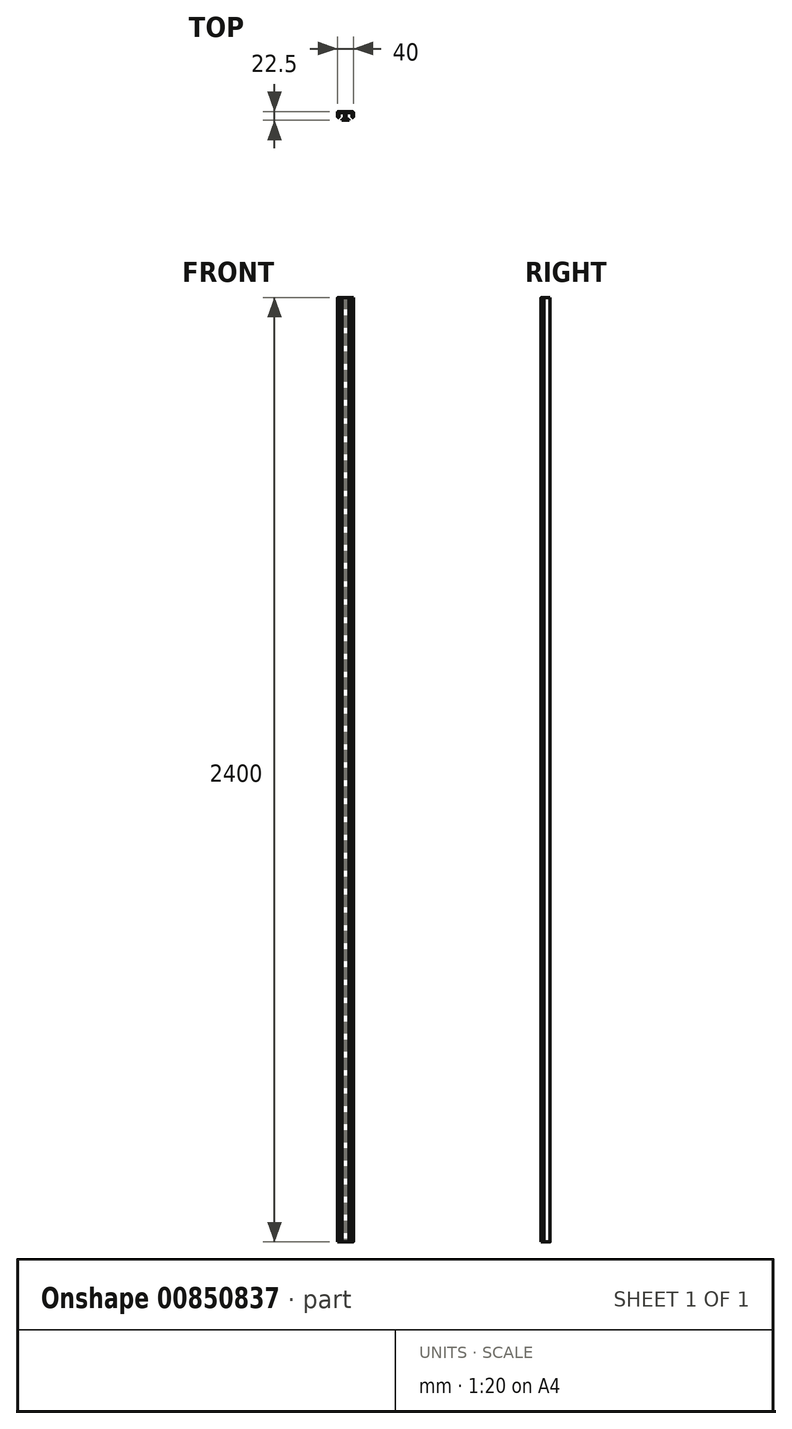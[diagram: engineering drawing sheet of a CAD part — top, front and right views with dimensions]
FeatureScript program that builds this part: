
annotation { "Feature Type Name" : "Feature", "Feature Type Description" : "" }
export const myFeature = defineFeature(function(context is Context, id is Id, definition is map)
    precondition{}
    {
        {
            var Q0;
            Q0=qCreatedBy(makeId("Top.planeOp"),FACE);
            var sketch = newSketch(context, id + "F0", { "sketchPlane" : qUnion([Q0])});
            skLineSegment(sketch, "E0", {"start": v(-20, 10) * mm, "end": v(20, 10) * mm});
            skLineSegment(sketch, "E1", {"start": v(20, 10) * mm, "end": v(20, -5) * mm});
            skLineSegment(sketch, "E2", {"start": v(-20, 10) * mm, "end": v(-20, -5) * mm});
            skLineSegment(sketch, "E3.0", {"start": v(-17, 7) * mm, "end": v(-17, -5) * mm});
            skLineSegment(sketch, "E3.1", {"start": v(-17, 7) * mm, "end": v(-2, 7) * mm});
            skLineSegment(sketch, "E3.2", {"start": v(17, 7) * mm, "end": v(17, -5) * mm});
            skLineSegment(sketch, "E4", {"start": v(-20, -5) * mm, "end": v(-17, -5) * mm});
            skLineSegment(sketch, "E5", {"start": v(17, -5) * mm, "end": v(20, -5) * mm});
            skLineSegment(sketch, "E6", {"start": v(-2, 7) * mm, "end": v(-2, -9.5) * mm});
            skLineSegment(sketch, "E7", {"start": v(-2, -9.5) * mm, "end": v(-8.5, -9.5) * mm});
            skLineSegment(sketch, "E8", {"start": v(-8.5, -9.5) * mm, "end": v(-8.5, -12.5) * mm});
            skLineSegment(sketch, "E9", {"start": v(-8.5, -12.5) * mm, "end": v(0, -12.5) * mm});
            skLineSegment(sketch, "E10.MirrorCS", {"start": v(8.5, -12.5) * mm, "end": v(0, -12.5) * mm});
            skLineSegment(sketch, "E11.MirrorCS", {"start": v(8.5, -9.5) * mm, "end": v(8.5, -12.5) * mm});
            skLineSegment(sketch, "E12.MirrorCS", {"start": v(2, 7) * mm, "end": v(2, -9.5) * mm});
            skLineSegment(sketch, "E13.MirrorCS", {"start": v(2, -9.5) * mm, "end": v(8.5, -9.5) * mm});
            skLineSegment(sketch, "E14.trimOffspring", {"start": v(2, 7) * mm, "end": v(17, 7) * mm});
            skSolve(sketch);
        }
        {
            var Q0;
            Q0 = qSketchRegion(id + "F0", true);
            extrude(context, id + "F1", {"entities" : qUnion([Q0]), "depth" : 2400 * mm, "offsetDistance" : 25 * mm});
        }
        {
            var Q0;
            Q0=makeQuery(id+"F1.opExtrude","SWEPT_EDGE",EDGE,{"disambiguationData":[OSD([sQuery(id+"F0.wireOp",EDGE,"E0"),sQuery(id+"F0.wireOp",EDGE,"E2")])]});
            var Q1;
            Q1=makeQuery(id+"F1.opExtrude","SWEPT_EDGE",EDGE,{"disambiguationData":[OSD([sQuery(id+"F0.wireOp",EDGE,"E0"),sQuery(id+"F0.wireOp",EDGE,"E1")])]});
            fillet(context, id + "F2", {"entities" : qUnion([Q0, Q1]), "radius" : 2 * mm, "tangentPropagation" : true, "allowEdgeOverflow" : false});
        }
        {
            var Q0;
            Q0=makeQuery(id+"F1.opExtrude","SWEPT_EDGE",EDGE,{"disambiguationData":[OSD([sQuery(id+"F0.wireOp",EDGE,"E2"),sQuery(id+"F0.wireOp",EDGE,"E4")])]});
            var Q1;
            Q1=makeQuery(id+"F1.opExtrude","SWEPT_EDGE",EDGE,{"disambiguationData":[OSD([sQuery(id+"F0.wireOp",EDGE,"E3.0"),sQuery(id+"F0.wireOp",EDGE,"E4")])]});
            var Q2;
            Q2=makeQuery(id+"F1.opExtrude","SWEPT_EDGE",EDGE,{"disambiguationData":[OSD([sQuery(id+"F0.wireOp",EDGE,"E3.0"),sQuery(id+"F0.wireOp",EDGE,"E3.1")])]});
            var Q3;
            Q3=makeQuery(id+"F1.opExtrude","SWEPT_EDGE",EDGE,{"disambiguationData":[OSD([sQuery(id+"F0.wireOp",EDGE,"E8"),sQuery(id+"F0.wireOp",EDGE,"E9")])]});
            var Q4;
            Q4=makeQuery(id+"F1.opExtrude","SWEPT_EDGE",EDGE,{"disambiguationData":[OSD([sQuery(id+"F0.wireOp",EDGE,"E10.MirrorCS"),sQuery(id+"F0.wireOp",EDGE,"E11.MirrorCS")])]});
            var Q5;
            Q5=makeQuery(id+"F1.opExtrude","SWEPT_EDGE",EDGE,{"disambiguationData":[OSD([sQuery(id+"F0.wireOp",EDGE,"E11.MirrorCS"),sQuery(id+"F0.wireOp",EDGE,"E13.MirrorCS")])]});
            var Q6;
            Q6=makeQuery(id+"F1.opExtrude","SWEPT_EDGE",EDGE,{"disambiguationData":[OSD([sQuery(id+"F0.wireOp",EDGE,"E12.MirrorCS"),sQuery(id+"F0.wireOp",EDGE,"E14.trimOffspring")])]});
            var Q7;
            Q7=makeQuery(id+"F1.opExtrude","SWEPT_EDGE",EDGE,{"disambiguationData":[OSD([sQuery(id+"F0.wireOp",EDGE,"E3.2"),sQuery(id+"F0.wireOp",EDGE,"E5")])]});
            var Q8;
            Q8=makeQuery(id+"F1.opExtrude","SWEPT_EDGE",EDGE,{"disambiguationData":[OSD([sQuery(id+"F0.wireOp",EDGE,"E1"),sQuery(id+"F0.wireOp",EDGE,"E5")])]});
            var Q9;
            Q9=makeQuery(id+"F1.opExtrude","SWEPT_EDGE",EDGE,{"disambiguationData":[OSD([sQuery(id+"F0.wireOp",EDGE,"E3.2"),sQuery(id+"F0.wireOp",EDGE,"E14.trimOffspring")])]});
            var Q10;
            Q10=makeQuery(id+"F1.opExtrude","SWEPT_EDGE",EDGE,{"disambiguationData":[OSD([sQuery(id+"F0.wireOp",EDGE,"E3.1"),sQuery(id+"F0.wireOp",EDGE,"E6")])]});
            var Q11;
            Q11=makeQuery(id+"F1.opExtrude","SWEPT_EDGE",EDGE,{"disambiguationData":[OSD([sQuery(id+"F0.wireOp",EDGE,"E7"),sQuery(id+"F0.wireOp",EDGE,"E8")])]});
            var Q12;
            Q12=makeQuery(id+"F1.opExtrude","SWEPT_EDGE",EDGE,{"disambiguationData":[OSD([sQuery(id+"F0.wireOp",EDGE,"E6"),sQuery(id+"F0.wireOp",EDGE,"E7")])]});
            var Q13;
            Q13=makeQuery(id+"F1.opExtrude","SWEPT_EDGE",EDGE,{"disambiguationData":[OSD([sQuery(id+"F0.wireOp",EDGE,"E12.MirrorCS"),sQuery(id+"F0.wireOp",EDGE,"E13.MirrorCS")])]});
            fillet(context, id + "F3", {"entities" : qUnion([Q0, Q1, Q2, Q3, Q4, Q5, Q6, Q7, Q8, Q9, Q10, Q11, Q12, Q13]), "radius" : 1 * mm, "tangentPropagation" : true, "allowEdgeOverflow" : false});
        }
    });
